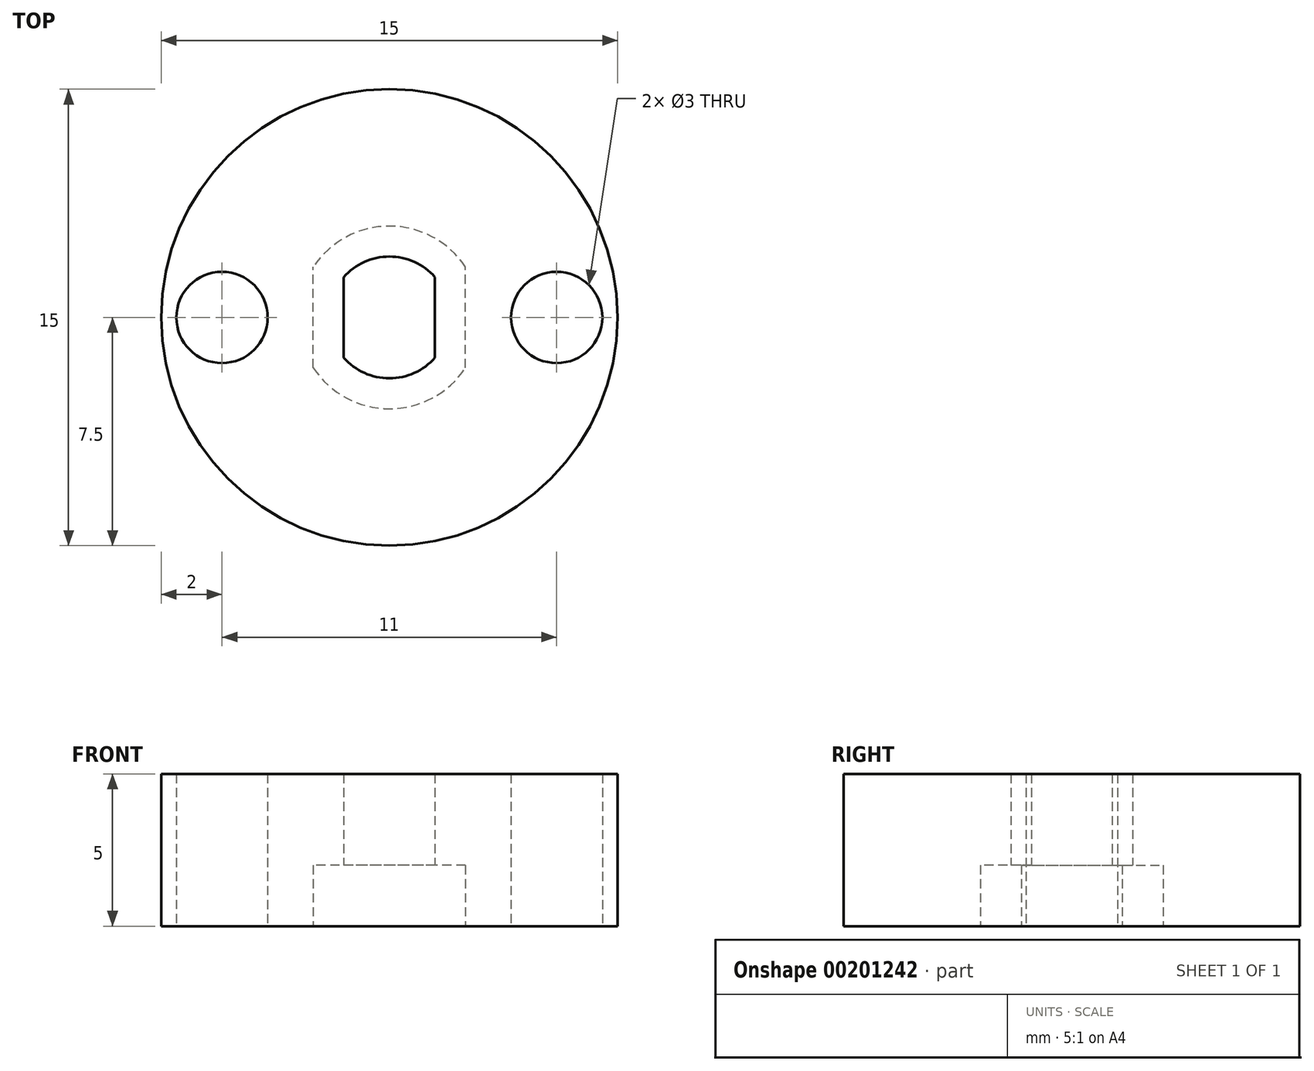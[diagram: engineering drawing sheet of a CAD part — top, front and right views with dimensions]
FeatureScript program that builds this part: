
annotation { "Feature Type Name" : "Feature", "Feature Type Description" : "" }
export const myFeature = defineFeature(function(context is Context, id is Id, definition is map)
    precondition{}
    {
        {
            var Q0;
            Q0=qCreatedBy(makeId("Top.planeOp"),FACE);
            var sketch = newSketch(context, id + "F0", { "sketchPlane" : qUnion([Q0])});
            skCircle(sketch, "E0", {"center": v(0, 0) * mm, "radius": 2 * mm});
            skCircle(sketch, "E1", {"center": v(0, 0) * mm, "radius": 7.5 * mm});
            skPoint(sketch, "E2", {"position": v(0, -5.5) * mm});
            skPoint(sketch, "E3", {"position": v(0, 5.5) * mm});
            skCircle(sketch, "E4", {"center": v(0, 5.5) * mm, "radius": 1.63 * mm});
            skCircle(sketch, "E5", {"center": v(0, -5.5) * mm, "radius": 1.63 * mm});
            skLineSegment(sketch, "E6.bottom", {"start": v(-1.5, 2.5) * mm, "end": v(1.5, 2.5) * mm});
            skLineSegment(sketch, "E6.top", {"start": v(-1.5, -2.5) * mm, "end": v(1.5, -2.5) * mm});
            skLineSegment(sketch, "E6.left", {"start": v(-1.5, 2.5) * mm, "end": v(-1.5, -2.5) * mm});
            skLineSegment(sketch, "E6.right", {"start": v(1.5, 2.5) * mm, "end": v(1.5, -2.5) * mm});
            skPoint(sketch, "E7", {"position": v(-5.5, 0) * mm});
            skPoint(sketch, "E7.positionSnap0", {"position": v(-1.5, 0) * mm});
            skPoint(sketch, "E8", {"position": v(5.5, 0) * mm});
            skPoint(sketch, "E8.positionSnap0", {"position": v(1.5, 0) * mm});
            skCircle(sketch, "E9", {"center": v(-5.5, 0) * mm, "radius": 1.5 * mm});
            skCircle(sketch, "E10", {"center": v(5.5, 0) * mm, "radius": 1.5 * mm});
            skSolve(sketch);
        }
        {
            var Q0;
            Q0 = qSketchRegion(id + "F0", true);
            var Q1;
            {var subQ5=sQuery(id+"F0.wireOp",EDGE,"E6.bottom");Q1=makeQuery(id+"F0.imprint","IMPRINT",FACE,{"disambiguationData":[TD([[makeQuery(id+"F0.imprint","IMPRINT",EDGE,{"derivedFrom":subQ5}),-1.0]])]});}
            var Q2;
            {var subQ5=sQuery(id+"F0.wireOp",EDGE,"E6.top");Q2=makeQuery(id+"F0.imprint","IMPRINT",FACE,{"disambiguationData":[TD([[makeQuery(id+"F0.imprint","IMPRINT",EDGE,{"derivedFrom":subQ5}),1.0]])]});}
            var Q3;
            {var subQ0=sQuery(id+"F0.wireOp",EDGE,"E6.left");var subQ1=sQuery(id+"F0.wireOp",EDGE,"E0");var subQ2=makeQuery(id+"F0.imprint","INTERSECT",VERTEX,{"disambiguationData":[OD(0.0)],"derivedFrom":[subQ1,subQ0]});Q3=makeQuery(id+"F0.imprint","IMPRINT",FACE,{"disambiguationData":[TD([[makeQuery(id+"F0.imprint","IMPRINT",EDGE,{"disambiguationData":[TD([[subQ2,-1.0]])],"derivedFrom":subQ1}),1.0]])]});}
            var Q4;
            {var subQ0=sQuery(id+"F0.wireOp",EDGE,"E6.right");var subQ1=sQuery(id+"F0.wireOp",EDGE,"E0");var subQ2=makeQuery(id+"F0.imprint","INTERSECT",VERTEX,{"disambiguationData":[OD(0.0)],"derivedFrom":[subQ1,subQ0]});Q4=makeQuery(id+"F0.imprint","IMPRINT",FACE,{"disambiguationData":[TD([[makeQuery(id+"F0.imprint","IMPRINT",EDGE,{"disambiguationData":[TD([[subQ2,1.0]])],"derivedFrom":subQ1}),1.0]])]});}
            var Q5;
            Q5=makeQuery(id+"F0.imprint","IMPRINT",FACE,{"disambiguationData":[TD([[makeQuery(id+"F0.imprint","IMPRINT",EDGE,{"derivedFrom":sQuery(id+"F0.wireOp",EDGE,"E4")}),1.0]])]});
            var Q6;
            Q6=makeQuery(id+"F0.imprint","IMPRINT",FACE,{"disambiguationData":[TD([[makeQuery(id+"F0.imprint","IMPRINT",EDGE,{"derivedFrom":sQuery(id+"F0.wireOp",EDGE,"E5")}),1.0]])]});
            extrude(context, id + "F1", {"entities" : qUnion([Q0, Q1, Q2, Q3, Q4, Q5, Q6]), "depth" : 5 * mm});
        }
        {
            var Q0;
            Q0=makeQuery(id+"F1.opExtrude","CAP_FACE",FACE,{"disambiguationData":[OSD([sQuery(id+"F0.wireOp",EDGE,"E0"),sQuery(id+"F0.wireOp",EDGE,"E1"),sQuery(id+"F0.wireOp",EDGE,"E4"),sQuery(id+"F0.wireOp",EDGE,"E5"),sQuery(id+"F0.wireOp",EDGE,"E6.left"),sQuery(id+"F0.wireOp",EDGE,"E6.right")])],"isStart":true});
            var sketch = newSketch(context, id + "F2", { "sketchPlane" : qUnion([Q0])});
            skCircle(sketch, "E11", {"center": v(0, 0) * mm, "radius": 3 * mm});
            skLineSegment(sketch, "E12.bottom", {"start": v(2.5, 3) * mm, "end": v(-2.5, 3) * mm});
            skLineSegment(sketch, "E12.top", {"start": v(2.5, -3) * mm, "end": v(-2.5, -3) * mm});
            skLineSegment(sketch, "E12.left", {"start": v(2.5, 3) * mm, "end": v(2.5, -3) * mm});
            skLineSegment(sketch, "E12.right", {"start": v(-2.5, 3) * mm, "end": v(-2.5, -3) * mm});
            skSolve(sketch);
        }
        {
            var Q0;
            {var subQ0=sQuery(id+"F0.wireOp",EDGE,"E6.left");Q0=makeQuery(id+"F2.imprint","IMPRINT",FACE,{"disambiguationData":[TD([[makeQuery(id+"F2.imprint","IMPRINT",EDGE,{"derivedFrom":makeQuery(id+"F1.opExtrude","CAP_EDGE",EDGE,{"disambiguationData":[OSD([subQ0])],"isStart":true})}),-1.0]])]});}
            var Q1;
            {var subQ4=sQuery(id+"F0.wireOp",EDGE,"E6.left");Q1=makeQuery(id+"F2.imprint","IMPRINT",FACE,{"disambiguationData":[TD([[makeQuery(id+"F2.imprint","IMPRINT",EDGE,{"derivedFrom":makeQuery(id+"F1.opExtrude","CAP_EDGE",EDGE,{"disambiguationData":[OSD([subQ4])],"isStart":true})}),1.0]])]});}
            extrude(context, id + "F3", {"entities" : qUnion([Q0, Q1]), "operationType" : NewBodyOperationType.REMOVE, "oppositeDirection" : true, "depth" : 2 * mm});
        }
    });
